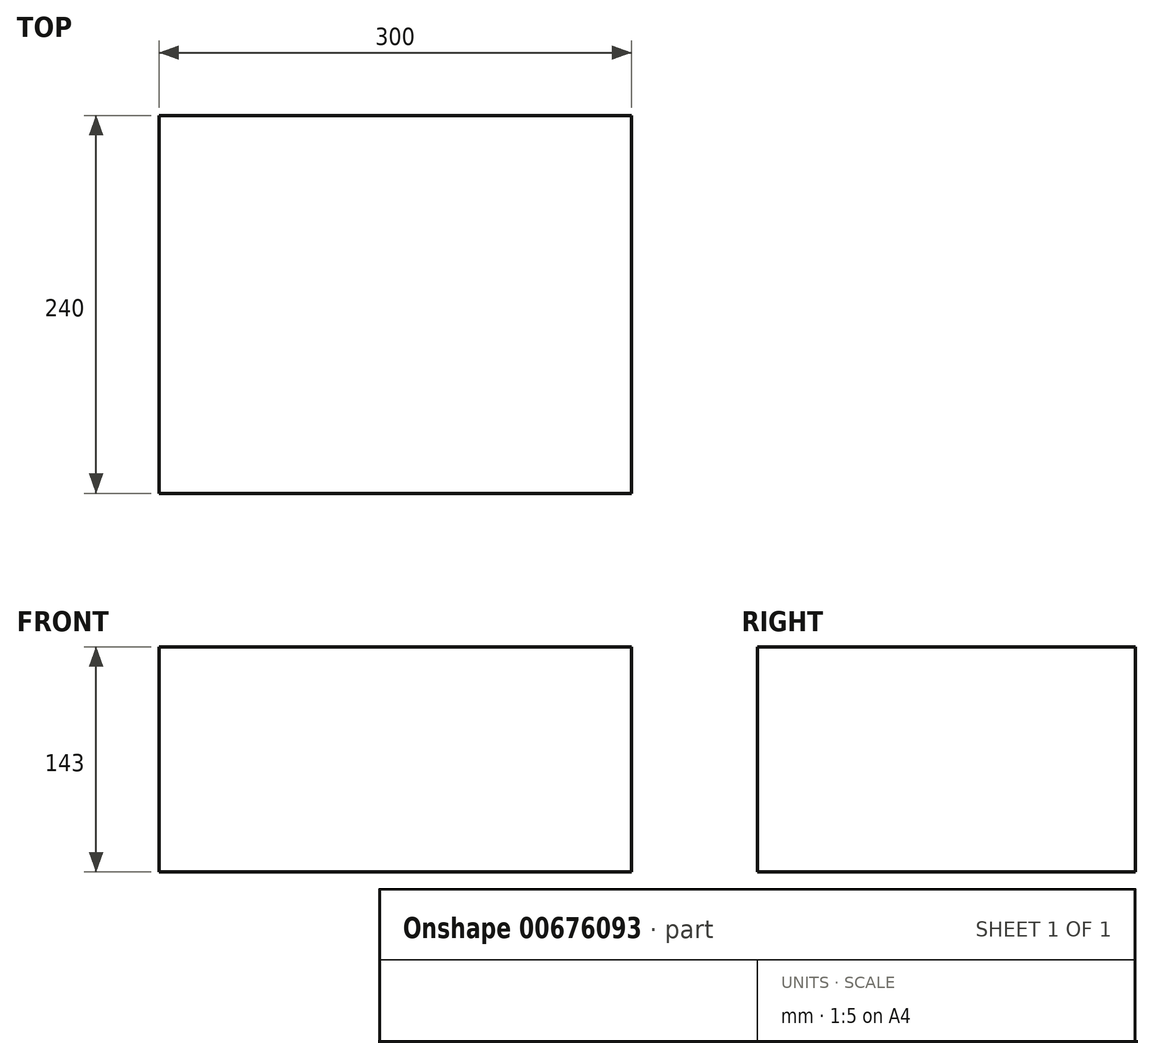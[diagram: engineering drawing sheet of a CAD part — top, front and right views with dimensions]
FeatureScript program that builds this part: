
annotation { "Feature Type Name" : "Feature", "Feature Type Description" : "" }
export const myFeature = defineFeature(function(context is Context, id is Id, definition is map)
    precondition{}
    {
        {
            var Q0;
            Q0=qCreatedBy(makeId("Front.planeOp"),FACE);
            var sketch = newSketch(context, id + "F0", { "sketchPlane" : qUnion([Q0])});
            skLineSegment(sketch, "E0.bottom", {"start": v(0, 0) * mm, "end": v(300, 0) * mm});
            skLineSegment(sketch, "E0.top", {"start": v(0, 143) * mm, "end": v(300, 143) * mm});
            skLineSegment(sketch, "E0.left", {"start": v(0, 0) * mm, "end": v(0, 143) * mm});
            skLineSegment(sketch, "E0.right", {"start": v(300, 0) * mm, "end": v(300, 143) * mm});
            skSolve(sketch);
        }
        {
            var Q0;
            Q0 = qSketchRegion(id + "F0", true);
            extrude(context, id + "F1", {"entities" : qUnion([Q0]), "depth" : 240 * mm, "offsetDistance" : 25 * mm});
        }
    });
